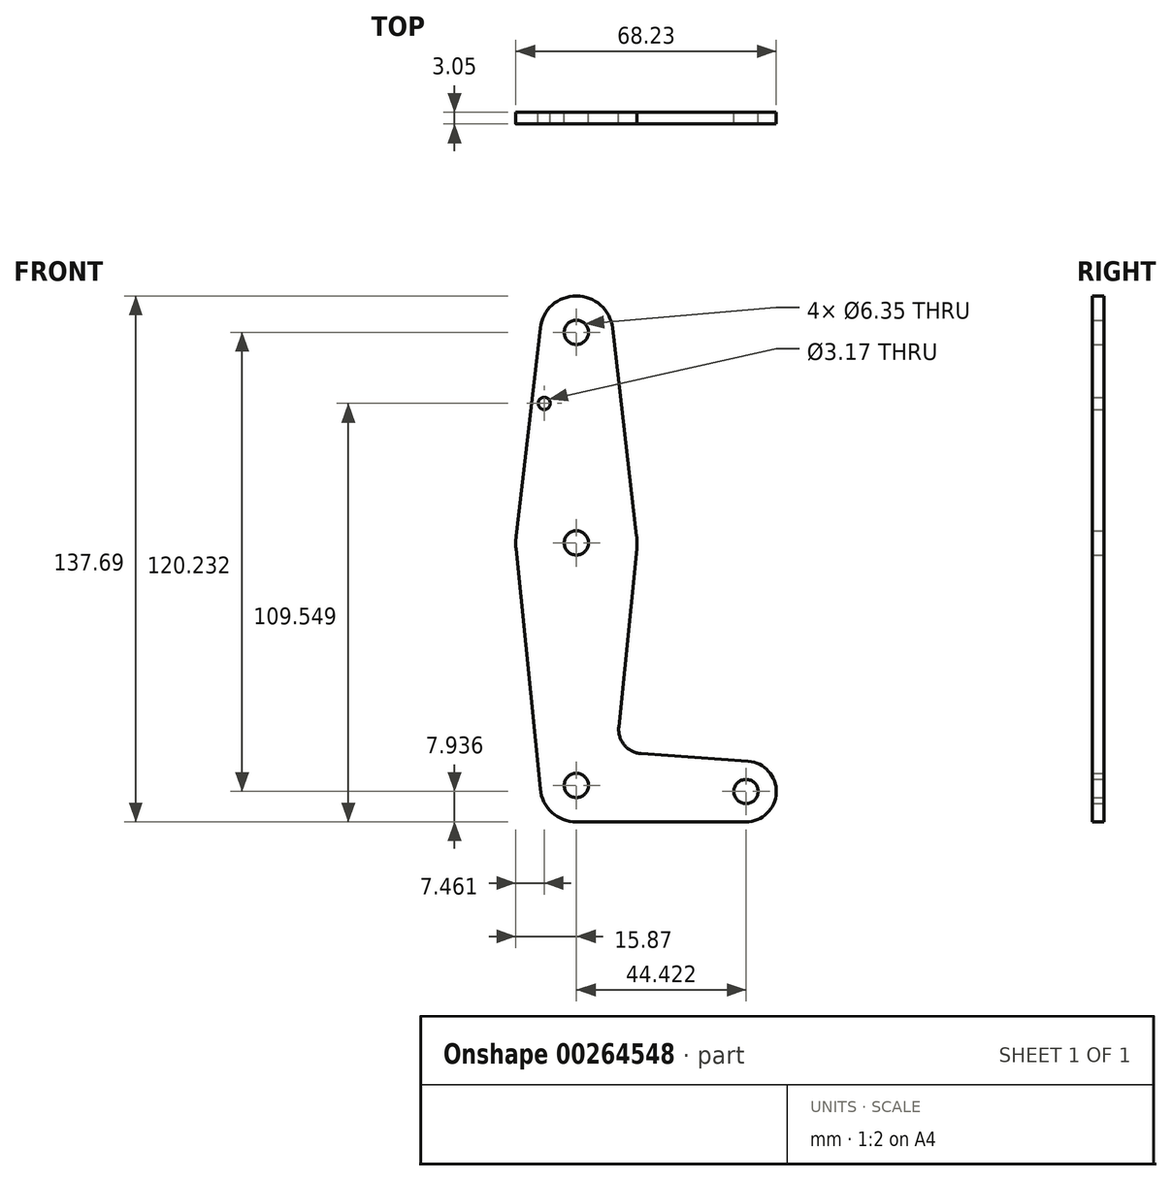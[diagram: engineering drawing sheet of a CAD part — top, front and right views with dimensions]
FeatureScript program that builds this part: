
annotation { "Feature Type Name" : "Feature", "Feature Type Description" : "" }
export const myFeature = defineFeature(function(context is Context, id is Id, definition is map)
    precondition{}
    {
        {
            var Q0;
            Q0=qCreatedBy(makeId("Front.planeOp"),FACE);
            var sketch = newSketch(context, id + "F0", { "sketchPlane" : qUnion([Q0])});
            skCircle(sketch, "E0", {"center": v(0, 51.99) * mm, "radius": 3.18 * mm});
            skCircle(sketch, "E1", {"center": v(0, 51.99) * mm, "radius": 9.52 * mm});
            skCircle(sketch, "E2", {"center": v(0, -66.66) * mm, "radius": 3.17 * mm});
            skCircle(sketch, "E3", {"center": v(0, -66.66) * mm, "radius": 9.53 * mm});
            skLineSegment(sketch, "E4", {"start": v(0, -66.66) * mm, "end": v(0, -3.16) * mm});
            skCircle(sketch, "E5", {"center": v(0, -3.16) * mm, "radius": 3.17 * mm});
            skCircle(sketch, "E6", {"center": v(0, -3.16) * mm, "radius": 15.88 * mm});
            skLineSegment(sketch, "E7", {"start": v(0, -3.16) * mm, "end": v(0, 61.51) * mm});
            skCircle(sketch, "E8", {"center": v(-8.4, 33.37) * mm, "radius": 1.59 * mm});
            skCircle(sketch, "E9", {"center": v(44.42, -68.24) * mm, "radius": 7.94 * mm});
            skLineSegment(sketch, "E10", {"start": v(9.46, 53.08) * mm, "end": v(15.77, -1.33) * mm});
            skLineSegment(sketch, "E11", {"start": v(-9.48, -67.6) * mm, "end": v(-15.8, -4.74) * mm});
            skLineSegment(sketch, "E12", {"start": v(15.8, -4.74) * mm, "end": v(11.11, -51.35) * mm});
            skLineSegment(sketch, "E13", {"start": v(16.98, -58.32) * mm, "end": v(44.99, -60.33) * mm});
            skLineSegment(sketch, "E14", {"start": v(0, -76.18) * mm, "end": v(44.42, -76.18) * mm});
            skArc(sketch, "E15.filletArc", {"start": v(11.11, -51.35) * mm, "mid": v(12.57, -56.08) * mm, "end": v(16.98, -58.32) * mm});
            skLineSegment(sketch, "E16", {"start": v(-9.46, 53.08) * mm, "end": v(-15.77, -1.33) * mm});
            skCircle(sketch, "E17", {"center": v(44.42, -68.24) * mm, "radius": 3.18 * mm});
            skSolve(sketch);
        }
        {
            var Q0;
            Q0 = qSketchRegion(id + "F0", true);
            extrude(context, id + "F1", {"entities" : qUnion([Q0]), "depth" : 3.05 * mm});
        }
    });
